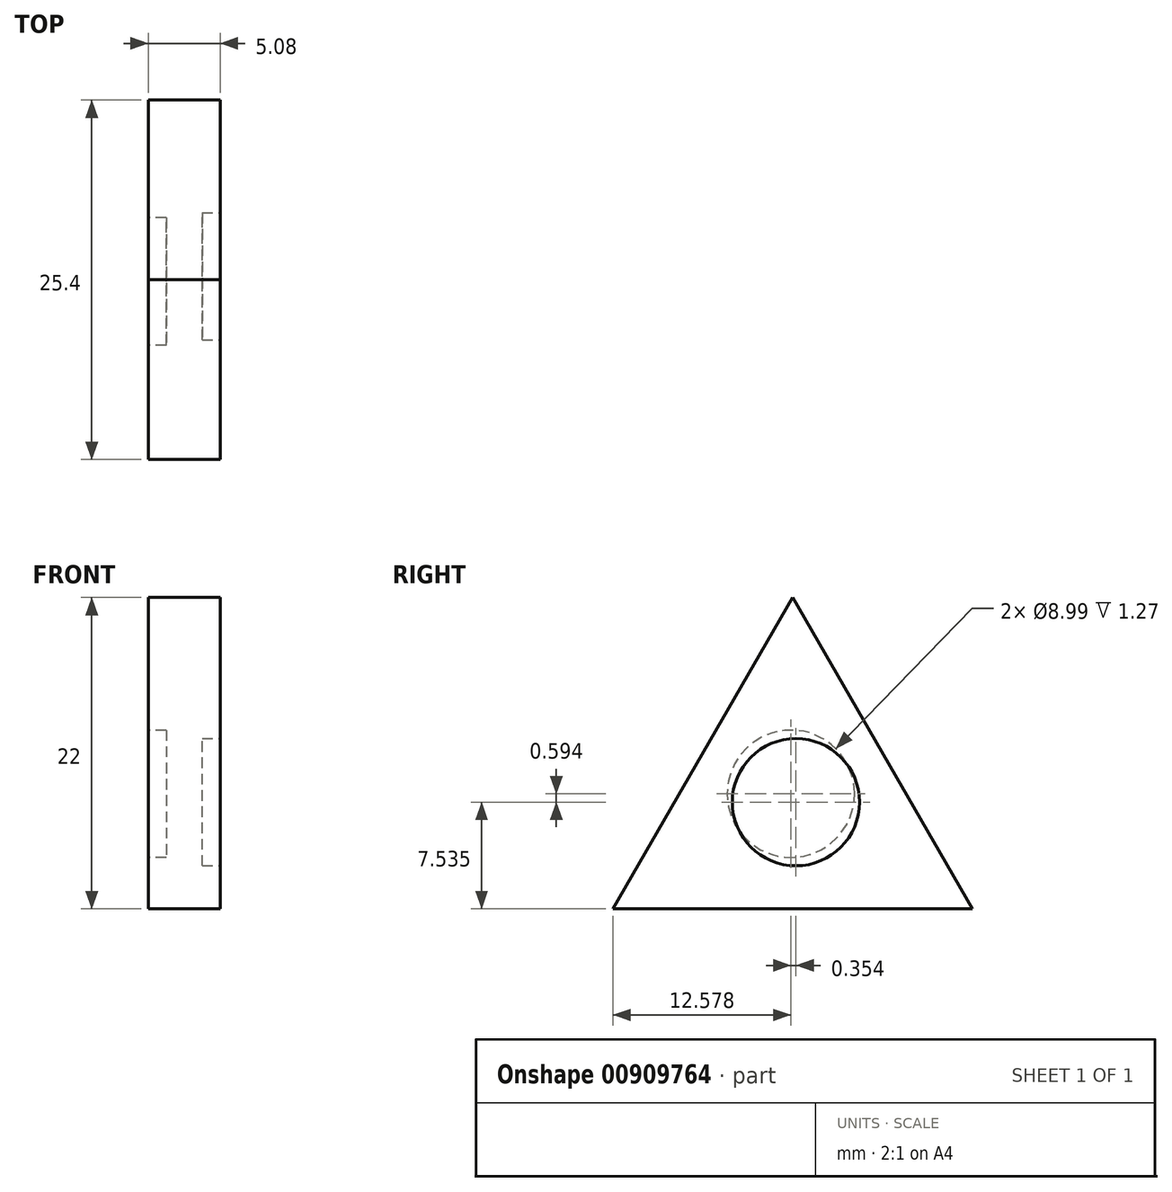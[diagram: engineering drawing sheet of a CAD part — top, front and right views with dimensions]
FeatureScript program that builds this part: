
annotation { "Feature Type Name" : "Feature", "Feature Type Description" : "" }
export const myFeature = defineFeature(function(context is Context, id is Id, definition is map)
    precondition{}
    {
        {
            var Q0;
            Q0=qCreatedBy(makeId("Right.planeOp"),FACE);
            var sketch = newSketch(context, id + "F0", { "sketchPlane" : qUnion([Q0])});
            skLineSegment(sketch, "E0.0", {"start": v(-12.7, 22) * mm, "end": v(0, 0) * mm});
            skLineSegment(sketch, "E0.1", {"start": v(0, 0) * mm, "end": v(-25.4, 0) * mm});
            skLineSegment(sketch, "E0.2", {"start": v(-25.4, 0) * mm, "end": v(-12.7, 22) * mm});
            skSolve(sketch);
        }
        {
            var Q0;
            Q0=makeQuery(id+"F0.imprint","IMPRINT",FACE,{"disambiguationData":[TD([[makeQuery(id+"F0.imprint","IMPRINT",EDGE,{"derivedFrom":sQuery(id+"F0.wireOp",EDGE,"E0.0")}),-1.0]])]});
            extrude(context, id + "F1", {"entities" : qUnion([Q0]), "depth" : 5.08 * mm, "offsetDistance" : 25.4 * mm});
        }
        {
            var Q0;
            Q0=makeQuery(id+"F1.opExtrude","CAP_FACE",FACE,{"disambiguationData":[OSD([sQuery(id+"F0.wireOp",EDGE,"E0.0"),sQuery(id+"F0.wireOp",EDGE,"E0.1"),sQuery(id+"F0.wireOp",EDGE,"E0.2")])],"isStart":false});
            var sketch = newSketch(context, id + "F2", { "sketchPlane" : qUnion([Q0])});
            skCircle(sketch, "E1", {"center": v(-12.47, 7.54) * mm, "radius": 4.5 * mm});
            skSolve(sketch);
        }
        {
            var Q0;
            Q0=makeQuery(id+"F2.imprint","IMPRINT",FACE,{"disambiguationData":[TD([[makeQuery(id+"F2.imprint","IMPRINT",EDGE,{"derivedFrom":sQuery(id+"F2.wireOp",EDGE,"E1")}),1.0]])]});
            extrude(context, id + "F3", {"entities" : qUnion([Q0]), "operationType" : NewBodyOperationType.REMOVE, "oppositeDirection" : true, "depth" : 1.27 * mm, "offsetDistance" : 25.4 * mm});
        }
        {
            var Q0;
            Q0=makeQuery(id+"F1.opExtrude","CAP_FACE",FACE,{"disambiguationData":[OSD([sQuery(id+"F0.wireOp",EDGE,"E0.0"),sQuery(id+"F0.wireOp",EDGE,"E0.1"),sQuery(id+"F0.wireOp",EDGE,"E0.2")])],"isStart":true});
            var sketch = newSketch(context, id + "F4", { "sketchPlane" : qUnion([Q0])});
            skCircle(sketch, "E2", {"center": v(12.82, 8.13) * mm, "radius": 4.5 * mm});
            skSolve(sketch);
        }
        {
            var Q0;
            Q0=makeQuery(id+"F4.imprint","IMPRINT",FACE,{"disambiguationData":[TD([[makeQuery(id+"F4.imprint","IMPRINT",EDGE,{"derivedFrom":sQuery(id+"F4.wireOp",EDGE,"E2")}),1.0]])]});
            extrude(context, id + "F5", {"entities" : qUnion([Q0]), "operationType" : NewBodyOperationType.REMOVE, "oppositeDirection" : true, "depth" : 1.27 * mm, "offsetDistance" : 25.4 * mm});
        }
    });
